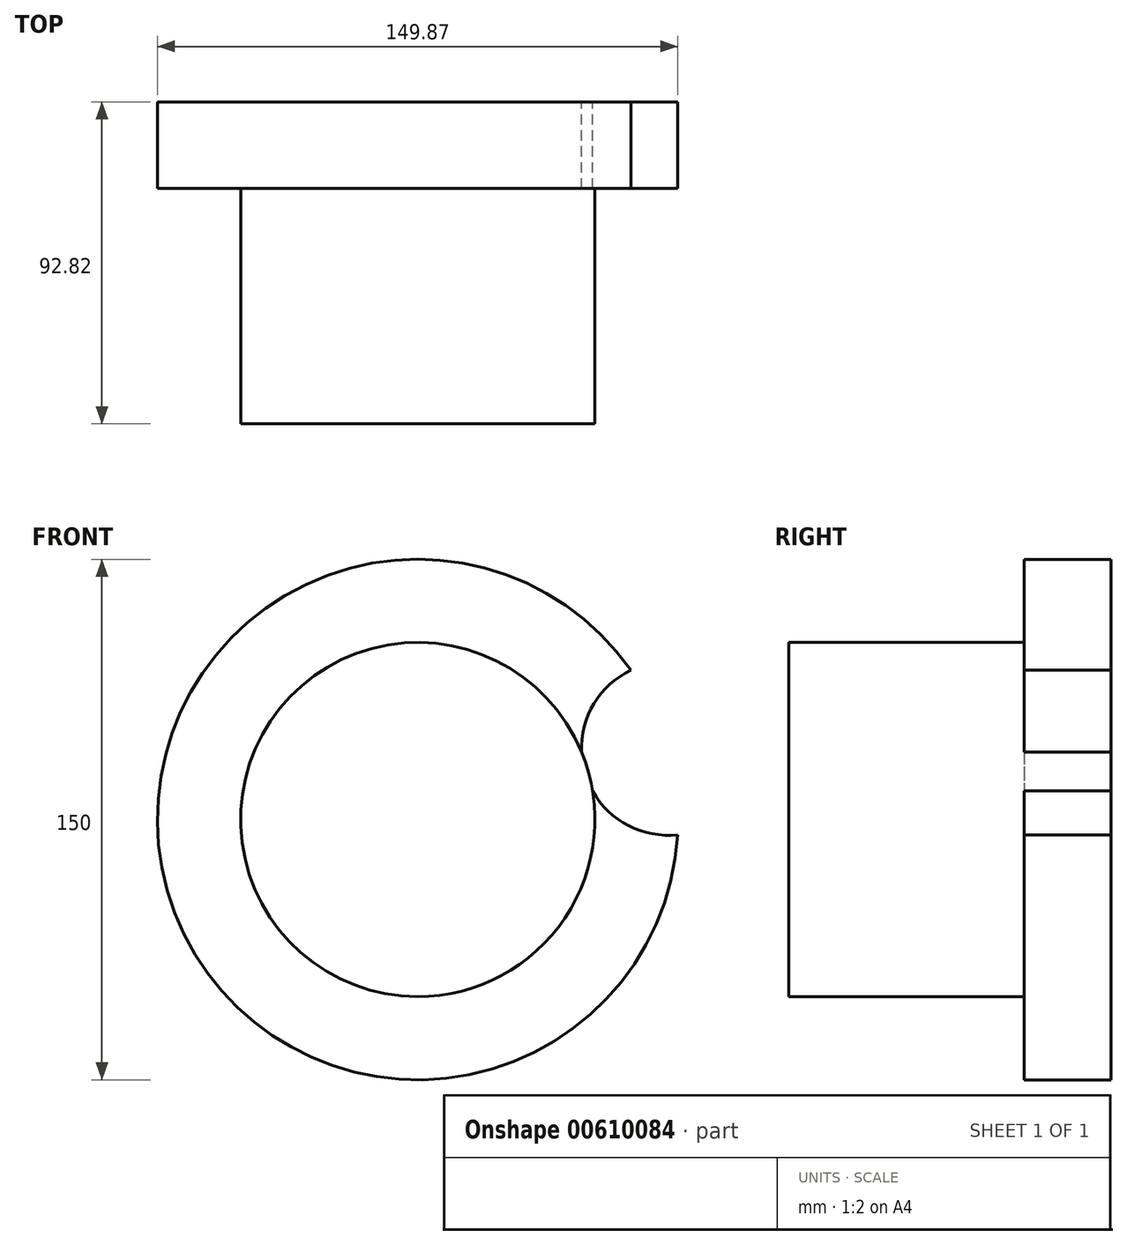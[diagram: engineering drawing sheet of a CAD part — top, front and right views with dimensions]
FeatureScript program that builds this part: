
annotation { "Feature Type Name" : "Feature", "Feature Type Description" : "" }
export const myFeature = defineFeature(function(context is Context, id is Id, definition is map)
    precondition{}
    {
        {
            var Q0;
            Q0=qCreatedBy(makeId("Front.planeOp"),FACE);
            var sketch = newSketch(context, id + "F0", { "sketchPlane" : qUnion([Q0])});
            skCircle(sketch, "E0", {"center": v(0, 0) * mm, "radius": 51.03 * mm});
            skSolve(sketch);
        }
        {
            var Q0;
            Q0=qCreatedBy(makeId("Front.planeOp"),FACE);
            var sketch = newSketch(context, id + "F1", { "sketchPlane" : qUnion([Q0])});
            skCircle(sketch, "E1", {"center": v(0, 0) * mm, "radius": 75 * mm});
            skCircle(sketch, "E2", {"center": v(72.15, 20.47) * mm, "radius": 25 * mm});
            skSolve(sketch);
        }
        {
            var Q0;
            {var subQ0=sQuery(id+"F1.wireOp",EDGE,"E2");var subQ1=sQuery(id+"F1.wireOp",EDGE,"E1");var subQ2=makeQuery(id+"F1.imprint","INTERSECT",VERTEX,{"disambiguationData":[OD(0.0)],"derivedFrom":[subQ1,subQ0]});Q0=makeQuery(id+"F1.imprint","IMPRINT",FACE,{"disambiguationData":[TD([[makeQuery(id+"F1.imprint","IMPRINT",EDGE,{"disambiguationData":[TD([[subQ2,1.0]])],"derivedFrom":subQ1}),1.0]])]});}
            extrude(context, id + "F2", {"entities" : qUnion([Q0]), "depth" : 25 * mm, "offsetDistance" : 25 * mm});
        }
        {
            var Q0;
            Q0=makeQuery(id+"F0.imprint","IMPRINT",FACE,{"disambiguationData":[TD([[makeQuery(id+"F0.imprint","IMPRINT",EDGE,{"derivedFrom":sQuery(id+"F0.wireOp",EDGE,"E0")}),1.0]])]});
            extrude(context, id + "F3", {"entities" : qUnion([Q0]), "operationType" : NewBodyOperationType.ADD, "depth" : 92.82 * mm, "offsetDistance" : 25 * mm});
        }
    });
